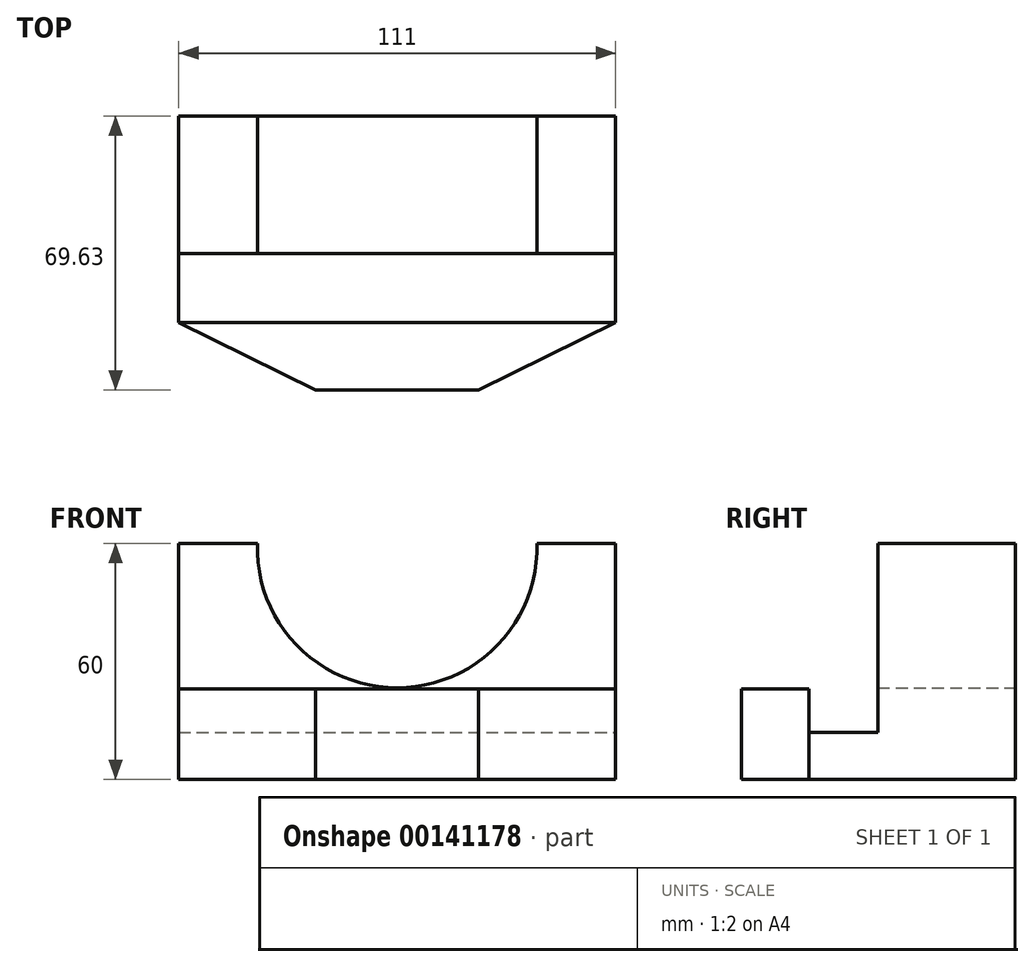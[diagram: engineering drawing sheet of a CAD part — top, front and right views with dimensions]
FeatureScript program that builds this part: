
annotation { "Feature Type Name" : "Feature", "Feature Type Description" : "" }
export const myFeature = defineFeature(function(context is Context, id is Id, definition is map)
    precondition{}
    {
        {
            var Q0;
            Q0=qCreatedBy(makeId("Front.planeOp"),FACE);
            var sketch = newSketch(context, id + "F0", { "sketchPlane" : qUnion([Q0])});
            skLineSegment(sketch, "E0", {"start": v(0, 0) * mm, "end": v(0, 60) * mm});
            skLineSegment(sketch, "E1", {"start": v(0, 60) * mm, "end": v(20, 60) * mm});
            skLineSegment(sketch, "E2", {"start": v(0, 0) * mm, "end": v(111, 0) * mm});
            skLineSegment(sketch, "E3", {"start": v(111, 0) * mm, "end": v(111, 60) * mm});
            skLineSegment(sketch, "E4", {"start": v(111, 60) * mm, "end": v(91, 60) * mm});
            skArc(sketch, "E5", {"start": v(20, 60) * mm, "mid": v(55.5, 23.34) * mm, "end": v(91, 60) * mm});
            skSolve(sketch);
        }
        {
            var Q0;
            Q0 = qSketchRegion(id + "F0", true);
            extrude(context, id + "F1", {"entities" : qUnion([Q0]), "depth" : 10 * mm, "hasSecondDirection" : true, "secondDirectionOppositeDirection" : true, "secondDirectionDepth" : 25 * mm});
        }
        {
            var Q0;
            Q0=qCreatedBy(makeId("Right.planeOp"),FACE);
            var sketch = newSketch(context, id + "F2", { "sketchPlane" : qUnion([Q0])});
            skLineSegment(sketch, "E6", {"start": v(-10.26, 12) * mm, "end": v(-27.45, 12) * mm});
            skLineSegment(sketch, "E7", {"start": v(-27.45, 12) * mm, "end": v(-27.45, 23) * mm});
            skLineSegment(sketch, "E8", {"start": v(-27.45, 23) * mm, "end": v(-44.63, 23) * mm});
            skLineSegment(sketch, "E9", {"start": v(-44.63, 23) * mm, "end": v(-44.63, 0) * mm});
            skLineSegment(sketch, "E10", {"start": v(-44.63, 0) * mm, "end": v(-27.17, 0) * mm});
            skLineSegment(sketch, "E11", {"start": v(-27.17, 0) * mm, "end": v(0, 0) * mm});
            skLineSegment(sketch, "E12", {"start": v(0, 0) * mm, "end": v(0, 12) * mm});
            skLineSegment(sketch, "E13", {"start": v(0, 12) * mm, "end": v(-10.26, 12) * mm});
            skSolve(sketch);
        }
        {
            var Q0;
            Q0 = qSketchRegion(id + "F2", true);
            extrude(context, id + "F3", {"entities" : qUnion([Q0]), "operationType" : NewBodyOperationType.ADD, "depth" : 111 * mm});
        }
        {
            var Q0;
            Q0=qCreatedBy(makeId("Top.planeOp"),FACE);
            var sketch = newSketch(context, id + "F4", { "sketchPlane" : qUnion([Q0])});
            skLineSegment(sketch, "E14", {"start": v(0, -27.45) * mm, "end": v(34.83, -44.63) * mm});
            skLineSegment(sketch, "E15", {"start": v(34.83, -44.63) * mm, "end": v(76.17, -44.63) * mm});
            skLineSegment(sketch, "E16", {"start": v(76.17, -44.63) * mm, "end": v(111, -27.45) * mm});
            skLineSegment(sketch, "E17", {"start": v(111, -27.45) * mm, "end": v(111, -44.63) * mm});
            skLineSegment(sketch, "E18", {"start": v(111, -44.63) * mm, "end": v(0, -44.63) * mm});
            skPoint(sketch, "E18.endSnap0", {"position": v(55.5, -44.63) * mm});
            skLineSegment(sketch, "E19", {"start": v(0, -44.63) * mm, "end": v(0, -27.45) * mm});
            skSolve(sketch);
        }
        {
            var Q0;
            Q0 = qSketchRegion(id + "F4", true);
            extrude(context, id + "F5", {"entities" : qUnion([Q0]), "operationType" : NewBodyOperationType.REMOVE, "endBound" : BoundingType.THROUGH_ALL, "depth" : 25 * mm});
        }
    });
